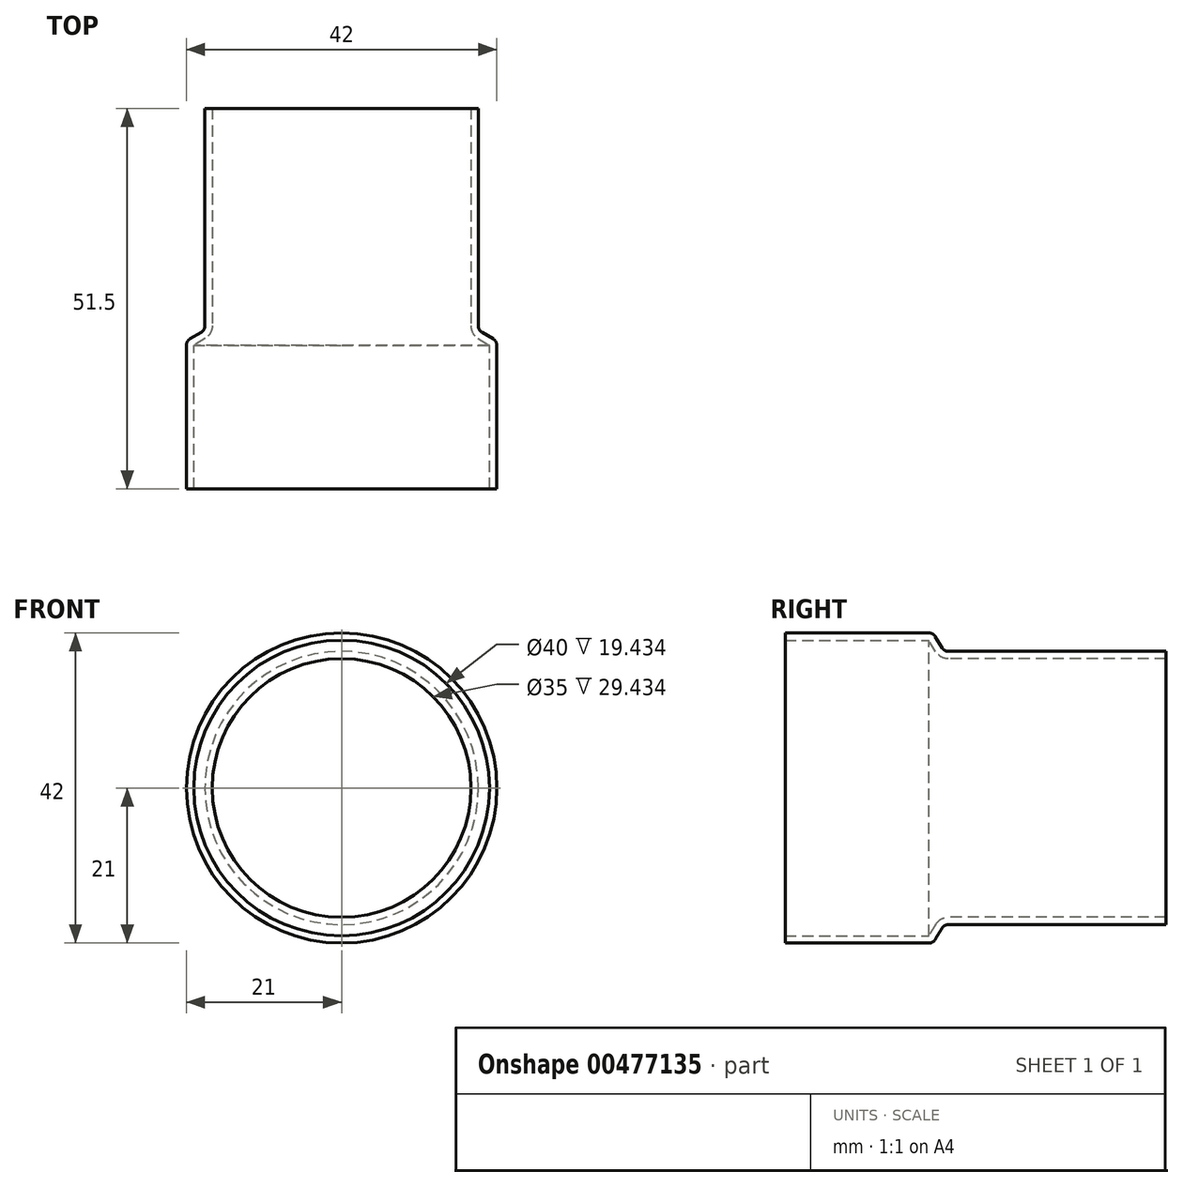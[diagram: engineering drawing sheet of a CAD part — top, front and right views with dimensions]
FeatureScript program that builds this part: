
annotation { "Feature Type Name" : "Feature", "Feature Type Description" : "" }
export const myFeature = defineFeature(function(context is Context, id is Id, definition is map)
    precondition{}
    {
        {
            var Q0;
            Q0=qCreatedBy(makeId("Front.planeOp"),FACE);
            var sketch = newSketch(context, id + "F0", { "sketchPlane" : qUnion([Q0])});
            skCircle(sketch, "E0", {"center": v(0, 0) * mm, "radius": 21 * mm});
            skSolve(sketch);
        }
        {
            var Q0;
            Q0 = qSketchRegion(id + "F0", true);
            extrude(context, id + "F1", {"entities" : qUnion([Q0]), "depth" : 20 * mm});
        }
        {
            var Q0;
            Q0=qCreatedBy(makeId("Front.planeOp"),FACE);
            cPlane(context, id + "F2", {"entities" : qUnion([Q0]), "cplaneType" : CPlaneType.OFFSET, "offset" : 1.5 * mm, "oppositeDirection" : true, "width" : 150 * mm, "height" : 150 * mm});
        }
        {
            var Q0;
            Q0=qCreatedBy(id+"F2.planeOp",FACE);
            var sketch = newSketch(context, id + "F3", { "sketchPlane" : qUnion([Q0])});
            skCircle(sketch, "E1", {"center": v(0, 0) * mm, "radius": 18.5 * mm});
            skSolve(sketch);
        }
        {
            var Q0;
            Q0 = qSketchRegion(id + "F3", true);
            extrude(context, id + "F4", {"entities" : qUnion([Q0]), "operationType" : NewBodyOperationType.ADD, "oppositeDirection" : true, "depth" : 30 * mm});
        }
        {
            var Q0;
            Q0=makeQuery(id+"F1.opExtrude","CAP_FACE",FACE,{"disambiguationData":[OSD([sQuery(id+"F0.wireOp",EDGE,"E0")])],"isStart":true});
            var Q1;
            Q1=makeQuery(id+"F4.opExtrude","CAP_FACE",FACE,{"disambiguationData":[OSD([sQuery(id+"F3.wireOp",EDGE,"E1")])],"isStart":true});
            loft(context, id + "F5", {"operationType" : NewBodyOperationType.ADD, "sheetProfilesArray" : [{ "sheetProfileEntities" : qUnion([Q0]) }, { "sheetProfileEntities" : qUnion([Q1]) }]});
        }
        {
            var Q0;
            {var subQ0=sQuery(id+"F0.wireOp",EDGE,"E0");Q0=makeQuery(id+"F5.boolean.opBoolean","MERGE",EDGE,{"derivedFrom":[makeQuery(id+"F1.opExtrude","CAP_EDGE",EDGE,{"disambiguationData":[OSD([subQ0])],"isStart":true}),makeQuery(id+"F5.opLoft","MID_CAP_EDGE",EDGE,{"disambiguationData":[OSD([subQ0])],"capPos":0.0})]});}
            var Q1;
            {var subQ0=sQuery(id+"F3.wireOp",EDGE,"E1");Q1=makeQuery(id+"F5.boolean.opBoolean","MERGE",EDGE,{"derivedFrom":[makeQuery(id+"F4.opExtrude","CAP_EDGE",EDGE,{"disambiguationData":[OSD([subQ0])],"isStart":true}),makeQuery(id+"F5.opLoft","MID_CAP_EDGE",EDGE,{"disambiguationData":[OSD([sQuery(id+"F0.wireOp",EDGE,"E0"),subQ0])],"capPos":1.0})]});}
            fillet(context, id + "F6", {"entities" : qUnion([Q0, Q1]), "radius" : 1 * mm, "tangentPropagation" : true, "allowEdgeOverflow" : false});
        }
        {
            var Q0;
            Q0=makeQuery(id+"F1.opExtrude","CAP_FACE",FACE,{"disambiguationData":[OSD([sQuery(id+"F0.wireOp",EDGE,"E0")])],"isStart":false});
            var Q1;
            Q1=makeQuery(id+"F4.opExtrude","CAP_FACE",FACE,{"disambiguationData":[OSD([sQuery(id+"F3.wireOp",EDGE,"E1")])],"isStart":false});
            shell(context, id + "F7", {"entities" : qUnion([Q0, Q1]), "thickness" : (1) * mm});
        }
    });
